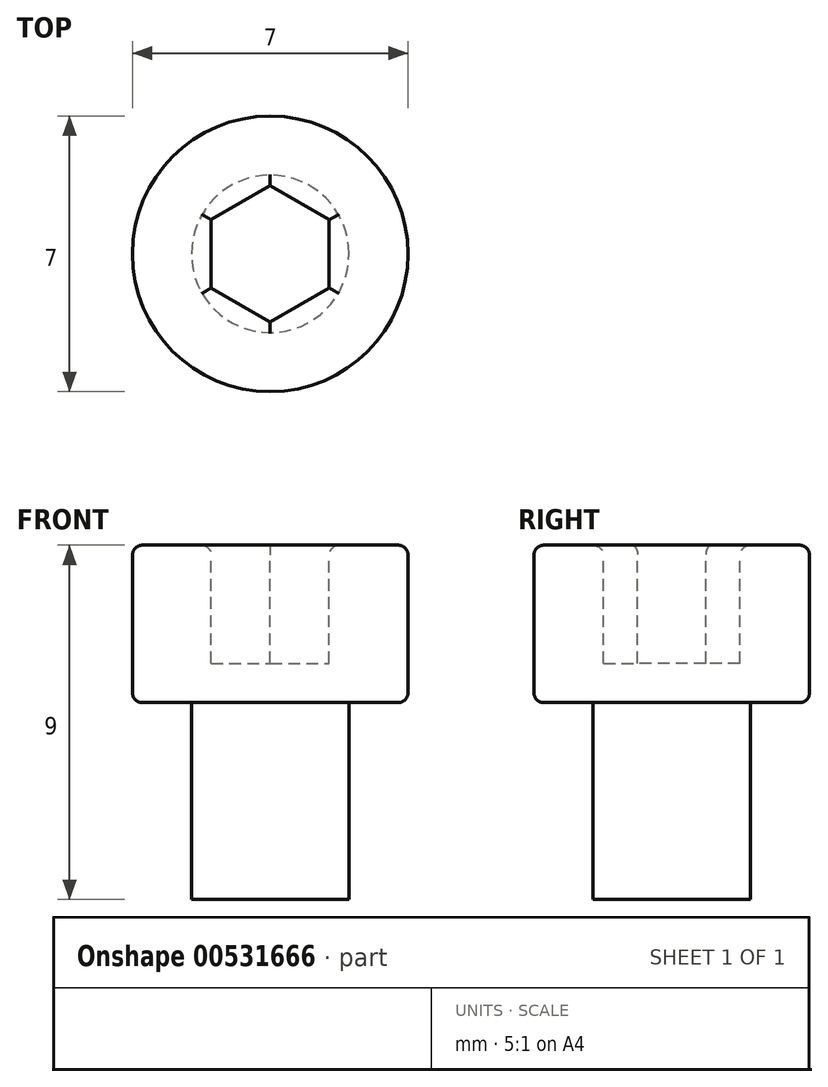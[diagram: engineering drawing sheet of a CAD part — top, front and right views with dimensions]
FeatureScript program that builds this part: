
annotation { "Feature Type Name" : "Feature", "Feature Type Description" : "" }
export const myFeature = defineFeature(function(context is Context, id is Id, definition is map)
    precondition{}
    {
        {
            var Q0;
            Q0=qCreatedBy(makeId("Top.planeOp"),FACE);
            var sketch = newSketch(context, id + "F0", { "sketchPlane" : qUnion([Q0])});
            skCircle(sketch, "E0", {"center": v(0, 0) * mm, "radius": 3.5 * mm});
            skSolve(sketch);
        }
        {
            var Q0;
            Q0 = qSketchRegion(id + "F0", true);
            extrude(context, id + "F1", {"entities" : qUnion([Q0]), "depth" : 4 * mm, "offsetDistance" : 25 * mm});
        }
        {
            var Q0;
            Q0=makeQuery(id+"F1.opExtrude","CAP_FACE",FACE,{"disambiguationData":[OSD([sQuery(id+"F0.wireOp",EDGE,"E0")])],"isStart":true});
            var sketch = newSketch(context, id + "F2", { "sketchPlane" : qUnion([Q0])});
            skCircle(sketch, "E1", {"center": v(0, 0) * mm, "radius": 2 * mm});
            skSolve(sketch);
        }
        {
            var Q0;
            Q0 = qSketchRegion(id + "F2", true);
            extrude(context, id + "F3", {"entities" : qUnion([Q0]), "operationType" : NewBodyOperationType.ADD, "depth" : 5 * mm, "offsetDistance" : 25 * mm});
        }
        {
            var Q0;
            Q0=makeQuery(id+"F1.opExtrude","CAP_FACE",FACE,{"disambiguationData":[OSD([sQuery(id+"F0.wireOp",EDGE,"E0")])],"isStart":false});
            var sketch = newSketch(context, id + "F4", { "sketchPlane" : qUnion([Q0])});
            skCircle(sketch, "E2.cCircle", {"center": v(0, 0) * mm, "radius": 1.5 * mm, "construction": true});
            skLineSegment(sketch, "E2.0", {"start": v(1.5, 0.87) * mm, "end": v(1.5, -0.87) * mm});
            skLineSegment(sketch, "E2.1", {"start": v(1.5, -0.87) * mm, "end": v(0, -1.73) * mm});
            skLineSegment(sketch, "E2.2", {"start": v(0, -1.73) * mm, "end": v(-1.5, -0.87) * mm});
            skLineSegment(sketch, "E2.3", {"start": v(-1.5, -0.87) * mm, "end": v(-1.5, 0.87) * mm});
            skLineSegment(sketch, "E2.4", {"start": v(-1.5, 0.87) * mm, "end": v(0, 1.73) * mm});
            skLineSegment(sketch, "E2.5", {"start": v(0, 1.73) * mm, "end": v(1.5, 0.87) * mm});
            skPoint(sketch, "E2.0.midPoint", {"position": v(1.5, 0) * mm});
            skSolve(sketch);
        }
        {
            var Q0;
            Q0 = qSketchRegion(id + "F4", true);
            extrude(context, id + "F5", {"entities" : qUnion([Q0]), "operationType" : NewBodyOperationType.REMOVE, "oppositeDirection" : true, "depth" : 3 * mm, "offsetDistance" : 25 * mm});
        }
        {
            var Q0;
            Q0=makeQuery(id+"F1.opExtrude","CAP_FACE",FACE,{"disambiguationData":[OSD([sQuery(id+"F0.wireOp",EDGE,"E0")])],"isStart":false});
            var Q1;
            Q1=makeQuery(id+"F1.opExtrude","CAP_EDGE",EDGE,{"disambiguationData":[OSD([sQuery(id+"F0.wireOp",EDGE,"E0")])],"isStart":true});
            fillet(context, id + "F6", {"entities" : qUnion([Q0, Q1]), "radius" : .25 * mm, "tangentPropagation" : true, "allowEdgeOverflow" : false});
        }
    });
